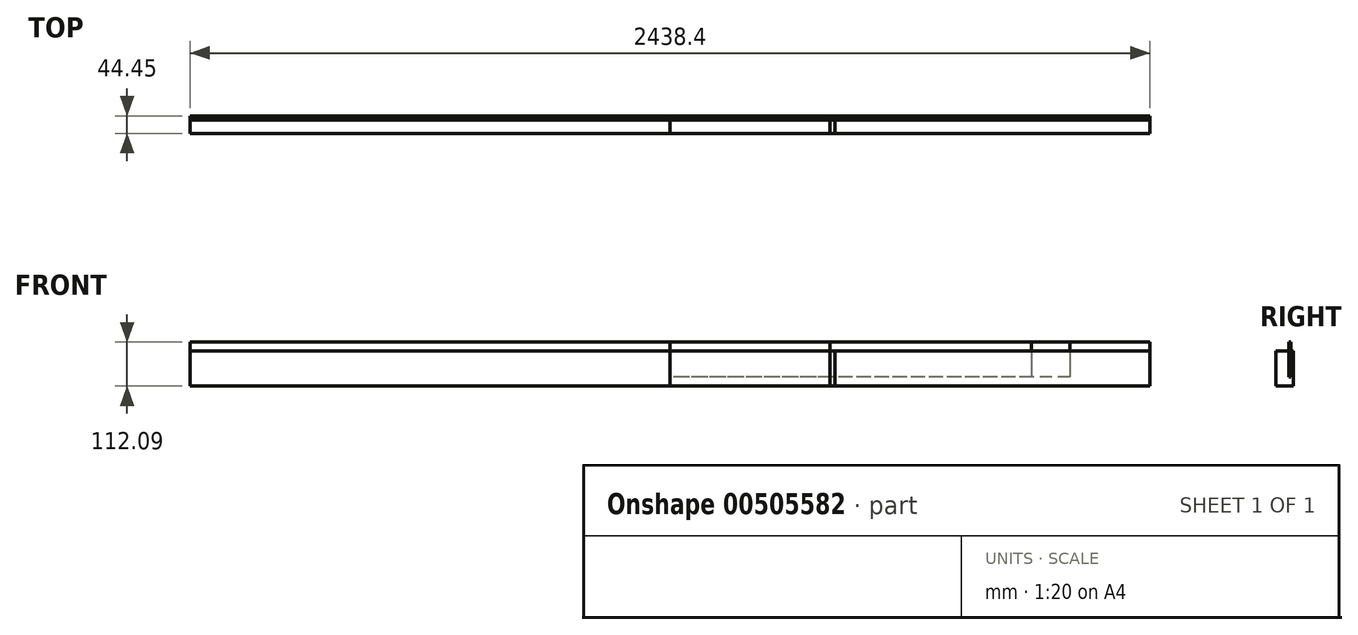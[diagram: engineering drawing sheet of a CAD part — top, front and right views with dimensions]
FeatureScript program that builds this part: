
annotation { "Feature Type Name" : "Feature", "Feature Type Description" : "" }
export const myFeature = defineFeature(function(context is Context, id is Id, definition is map)
    precondition{}
    {
        {
            var Q0;
            Q0=qCreatedBy(makeId("Right.planeOp"),FACE);
            var sketch = newSketch(context, id + "F0", { "sketchPlane" : qUnion([Q0])});
            skLineSegment(sketch, "E0.bottom", {"start": v(-9.41, 78.68) * mm, "end": v(-4.65, 78.68) * mm});
            skLineSegment(sketch, "E0.top", {"start": v(-9.41, -10.22) * mm, "end": v(-4.65, -10.22) * mm});
            skLineSegment(sketch, "E0.left", {"start": v(-9.41, 78.68) * mm, "end": v(-9.41, -10.22) * mm});
            skLineSegment(sketch, "E0.right", {"start": v(-4.65, 78.68) * mm, "end": v(-4.65, -10.22) * mm});
            skSolve(sketch);
        }
        {
            var Q0;
            Q0=makeQuery(id+"F0.imprint","IMPRINT",FACE,{"disambiguationData":[TD([[makeQuery(id+"F0.imprint","IMPRINT",EDGE,{"derivedFrom":sQuery(id+"F0.wireOp",EDGE,"E0.bottom")}),-1.0]])]});
            extrude(context, id + "F1", {"entities" : qUnion([Q0]), "endBound" : BoundingType.SYMMETRIC, "depth" : 2438.4 * mm});
        }
        {
            var Q0;
            Q0=qCreatedBy(makeId("Right.planeOp"),FACE);
            var sketch = newSketch(context, id + "F2", { "sketchPlane" : qUnion([Q0])});
            skLineSegment(sketch, "E1.bottom", {"start": v(-43.02, 55.49) * mm, "end": v(1.43, 55.49) * mm});
            skLineSegment(sketch, "E1.top", {"start": v(-43.02, -33.41) * mm, "end": v(1.43, -33.41) * mm});
            skLineSegment(sketch, "E1.left", {"start": v(-43.02, 55.49) * mm, "end": v(-43.02, -33.41) * mm});
            skLineSegment(sketch, "E1.right", {"start": v(1.43, 55.49) * mm, "end": v(1.43, -33.41) * mm});
            skSolve(sketch);
        }
        {
            var Q0;
            Q0=makeQuery(id+"F2.imprint","IMPRINT",FACE,{"disambiguationData":[TD([[makeQuery(id+"F2.imprint","IMPRINT",EDGE,{"derivedFrom":sQuery(id+"F2.wireOp",EDGE,"E1.bottom")}),-1.0]])]});
            extrude(context, id + "F3", {"entities" : qUnion([Q0]), "endBound" : BoundingType.SYMMETRIC, "oppositeDirection" : true, "depth" : 2438.4 * mm, "offsetDistance" : 25.4 * mm});
        }
        {
            var Q0;
            Q0 = qSketchRegion(id + "F2", true);
            extrude(context, id + "F4", {"entities" : qUnion([Q0]), "depth" : 1219.2 * mm});
        }
        {
            var Q0;
            Q0 = qSketchRegion(id + "F0", true);
            extrude(context, id + "F5", {"entities" : qUnion([Q0]), "depth" : 1016 * mm});
        }
        {
            var Q0;
            Q0 = qSketchRegion(id + "F0", true);
            extrude(context, id + "F6", {"entities" : qUnion([Q0]), "depth" : 406.4 * mm});
        }
        {
            var Q0;
            Q0 = qSketchRegion(id + "F0", true);
            extrude(context, id + "F7", {"entities" : qUnion([Q0]), "depth" : 917.57 * mm});
        }
        {
            var Q0;
            Q0 = qSketchRegion(id + "F2", true);
            extrude(context, id + "F8", {"entities" : qUnion([Q0]), "depth" : 419.1 * mm});
        }
        {
            var Q0;
            Q0 = qSketchRegion(id + "F2", true);
            extrude(context, id + "F9", {"entities" : qUnion([Q0]), "depth" : 406.4 * mm});
        }
    });
